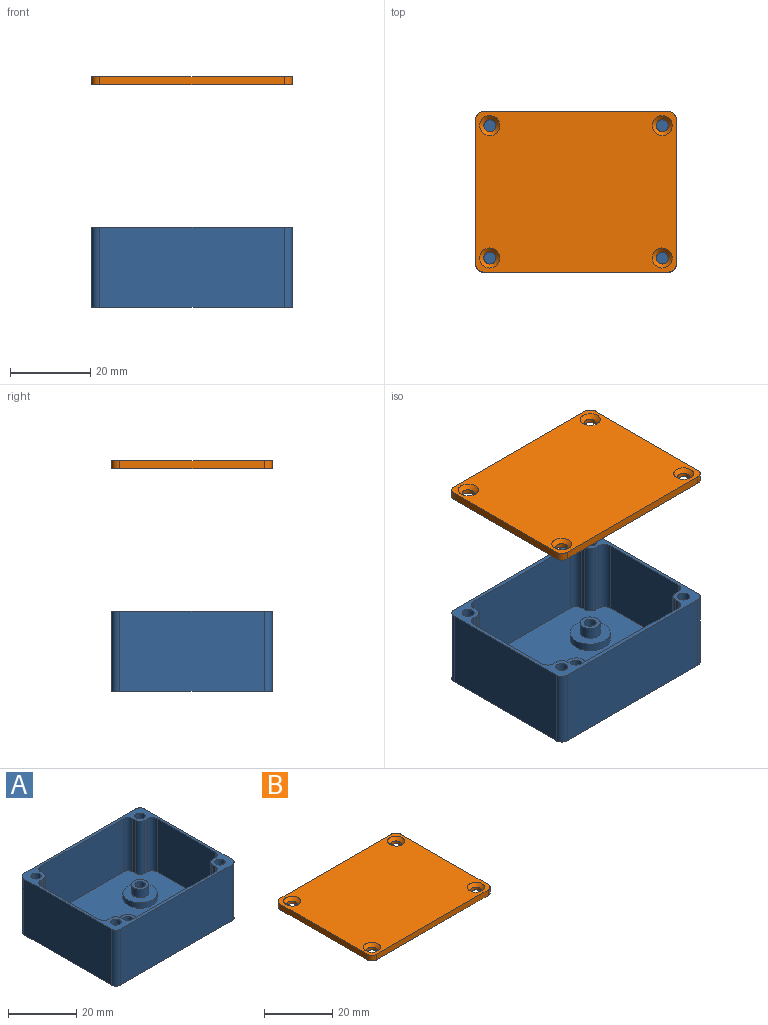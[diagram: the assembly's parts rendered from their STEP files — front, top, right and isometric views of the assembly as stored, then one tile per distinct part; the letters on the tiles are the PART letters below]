
ASSEMBLY  parts=2 mates=1
PART A: 67 faces, bbox 50x40x20 mm
  f0: cylinder r=1.5mm len=4mm, axis (0,0,-1), area 37.7mm2, adj f30,f50
  f1: cylinder r=1.5mm len=4mm, axis (0,0,-1), area 37.7mm2, adj f32,f43
  f2: plane 48x38mm, normal (0,0,1), area 1563.5mm2, adj f3,f4,f5,f6,f13,f14,f15,f16
  f3: plane 24x19mm, normal (-1,0,0), area 456mm2, adj f2,f7,f60,f61
  f4: plane 34x19mm, normal (0,1,0), area 646mm2, adj f2,f7,f56,f58
  f5: plane 34x19mm, normal (0,-1,0), area 646mm2, adj f2,f7,f62,f64
  f6: plane 24x19mm, normal (1,0,0), area 456mm2, adj f2,f7,f57,f66
  f7: plane 50x40mm, normal (0,0,1), area 247.7mm2, adj f3,f4,f5,f6,f8,f9,f10,f11
  f8: plane 46x20mm, normal (0,1,0), area 920mm2, adj f7,f12,f51,f54
  f9: plane 36x20mm, normal (-1,0,0), area 720mm2, adj f7,f12,f51,f52
  f10: plane 46x20mm, normal (0,-1,0), area 920mm2, adj f7,f12,f52,f53
  f11: plane 36x20mm, normal (1,0,0), area 720mm2, adj f7,f12,f53,f54
  f12: plane 50x40mm, normal (0,0,-1), area 1949.8mm2, adj f8,f9,f10,f11,f37,f38,f39,f40
  f13: plane 19x1mm, normal (0,-1,0), area 19mm2, adj f2,f7,f65,f66
  f14: plane 19x1mm, normal (1,0,0), area 19mm2, adj f2,f7,f64,f65
  f15: plane 19x1mm, normal (0,1,0), area 19mm2, adj f2,f7,f55,f57
  f16: plane 19x1mm, normal (1,0,0), area 19mm2, adj f2,f7,f55,f56
  f17: plane 19x1mm, normal (0,-1,0), area 19mm2, adj f2,f7,f61,f63
  f18: plane 19x1mm, normal (-1,0,0), area 19mm2, adj f2,f7,f62,f63
  f19: plane 19x1mm, normal (0,1,0), area 19mm2, adj f2,f7,f59,f60
  f20: plane 19x1mm, normal (-1,0,0), area 19mm2, adj f2,f7,f58,f59
  f21: cylinder r=1.5mm len=10mm, axis (0,0,1), area 94.2mm2, adj f7,f22
  f22: plane 3x3mm, normal (0,0,1), area 7.1mm2, adj f21
  f23: cylinder r=1.5mm len=10mm, axis (0,0,1), area 94.2mm2, adj f7,f24
  f24: plane 3x3mm, normal (0,0,1), area 7.1mm2, adj f23
  f25: cylinder r=1.5mm len=10mm, axis (0,0,1), area 94.2mm2, adj f7,f26
  f26: plane 3x3mm, normal (0,0,1), area 7.1mm2, adj f25
  f27: cylinder r=1.5mm len=10mm, axis (0,0,1), area 94.2mm2, adj f7,f28
  f28: plane 3x3mm, normal (0,0,1), area 7.1mm2, adj f27
  f29: cylinder r=2.5mm len=5mm, axis (0,0,-1), area 47.1mm2, adj f30,f34
  f30: plane 5x5mm, normal (0,0,1), area 12.6mm2, adj f0,f29
  f31: cylinder r=2.5mm len=5mm, axis (0,0,-1), area 47.1mm2, adj f32,f36
  f32: plane 5x5mm, normal (0,0,1), area 12.6mm2, adj f1,f31
  f33: cylinder r=5mm len=10mm, axis (0,0,-1), area 62.8mm2, adj f2,f34
  f34: plane 10x10mm, normal (0,0,1), area 58.9mm2, adj f29,f33
  f35: cylinder r=5mm len=10mm, axis (0,0,-1), area 62.8mm2, adj f2,f36
  f36: plane 10x10mm, normal (0,0,1), area 58.9mm2, adj f31,f35
  f37: plane 3x2mm, normal (1,0,0), area 6mm2, adj f12,f38,f42,f43
  f38: plane 2.6x2mm, normal (0.5,-0.87,0), area 6mm2, adj f12,f37,f39,f43
  f39: plane 2.6x2mm, normal (-0.5,-0.87,0), area 6mm2, adj f12,f38,f40,f43
  f40: plane 3x2mm, normal (-1,0,0), area 6mm2, adj f12,f39,f41,f43
  f41: plane 2.6x2mm, normal (-0.5,0.87,0), area 6mm2, adj f12,f40,f42,f43
  f42: plane 2.6x2mm, normal (0.5,0.87,0), area 6mm2, adj f12,f37,f41,f43
  f43: plane 6x5.2mm, normal (0,0,-1), area 16.3mm2, adj f1,f37,f38,f39,f40,f41,f42
  f44: plane 2.93x2mm, normal (0.98,0.21,0), area 6mm2, adj f12,f45,f49,f50
  f45: plane 2.23x2.01mm, normal (0.67,-0.74,0), area 6mm2, adj f12,f44,f46,f50
  f46: plane 2.85x2mm, normal (-0.31,-0.95,0), area 6mm2, adj f12,f45,f47,f50
  f47: plane 2.93x2mm, normal (-0.98,-0.21,0), area 6mm2, adj f12,f46,f48,f50
  f48: plane 2.23x2.01mm, normal (-0.67,0.74,0), area 6mm2, adj f12,f47,f49,f50
  f49: plane 2.85x2mm, normal (0.31,0.95,0), area 6mm2, adj f12,f44,f48,f50
  f50: plane 5.87x5.71mm, normal (0,0,-1), area 16.3mm2, adj f0,f44,f45,f46,f47,f48,f49
  f51: cylinder r=2mm len=20mm, axis (0,0,1), area 62.8mm2, adj f7,f8,f9,f12
  f52: cylinder r=2mm len=20mm, axis (0,0,-1), area 62.8mm2, adj f7,f9,f10,f12
  f53: cylinder r=2mm len=20mm, axis (0,0,1), area 62.8mm2, adj f7,f10,f11,f12
  f54: cylinder r=2mm len=20mm, axis (0,0,-1), area 62.8mm2, adj f7,f8,f11,f12
  f55: cylinder r=2mm len=19mm, axis (0,0,1), area 59.7mm2, adj f2,f7,f15,f16
  f56: cylinder r=2mm len=19mm, axis (0,0,1), area 59.7mm2, adj f2,f4,f7,f16
  f57: cylinder r=2mm len=19mm, axis (0,0,-1), area 59.7mm2, adj f2,f6,f7,f15
  f58: cylinder r=2mm len=19mm, axis (0,0,-1), area 59.7mm2, adj f2,f4,f7,f20
  f59: cylinder r=2mm len=19mm, axis (0,0,1), area 59.7mm2, adj f2,f7,f19,f20
  f60: cylinder r=2mm len=19mm, axis (0,0,-1), area 59.7mm2, adj f2,f3,f7,f19
  f61: cylinder r=2mm len=19mm, axis (0,0,1), area 59.7mm2, adj f2,f3,f7,f17
  f62: cylinder r=2mm len=19mm, axis (0,0,-1), area 59.7mm2, adj f2,f5,f7,f18
  f63: cylinder r=2mm len=19mm, axis (0,0,1), area 59.7mm2, adj f2,f7,f17,f18
  f64: cylinder r=2mm len=19mm, axis (0,0,1), area 59.7mm2, adj f2,f5,f7,f14
  f65: cylinder r=2mm len=19mm, axis (0,0,1), area 59.7mm2, adj f2,f7,f13,f14
  f66: cylinder r=2mm len=19mm, axis (0,0,1), area 59.7mm2, adj f2,f6,f7,f13
PART B: 18 faces, bbox 50x40x2 mm
  f0: plane 36x2mm, normal (-1,0,0), area 72mm2, adj f4,f5,f14,f17
  f1: plane 46x2mm, normal (0,-1,0), area 92mm2, adj f4,f5,f14,f15
  f2: plane 36x2mm, normal (1,0,0), area 72mm2, adj f4,f5,f15,f16
  f3: plane 46x2mm, normal (0,1,0), area 92mm2, adj f4,f5,f16,f17
  f4: plane 50x40mm, normal (0,0,1), area 1918mm2, adj f0,f1,f2,f3,f10,f11,f12,f13
  f5: plane 50x40mm, normal (0,0,-1), area 1968.3mm2, adj f0,f1,f2,f3,f6,f7,f8,f9
  f6: cylinder r=1.5mm len=3mm, axis (0,0,1), area 9.4mm2, adj f5,f13
  f7: cylinder r=1.5mm len=3mm, axis (0,0,1), area 9.4mm2, adj f5,f12
  f8: cylinder r=1.5mm len=3mm, axis (0,0,1), area 9.4mm2, adj f5,f10
  f9: cylinder r=1.5mm len=3mm, axis (0,0,1), area 9.4mm2, adj f5,f11
  f10: cone r=1.5mm half-angle=45deg, axis (0,0,1), area 17.8mm2, adj f4,f8
  f11: cone r=1.5mm half-angle=45deg, axis (0,0,1), area 17.8mm2, adj f4,f9
  f12: cone r=1.5mm half-angle=45deg, axis (0,0,1), area 17.8mm2, adj f4,f7
  f13: cone r=1.5mm half-angle=45deg, axis (0,0,1), area 17.8mm2, adj f4,f6
  f14: cylinder r=2mm len=2mm, axis (0,0,1), area 6.3mm2, adj f0,f1,f4,f5
  f15: cylinder r=2mm len=2mm, axis (0,0,-1), area 6.3mm2, adj f1,f2,f4,f5
  f16: cylinder r=2mm len=2mm, axis (0,0,1), area 6.3mm2, adj f2,f3,f4,f5
  f17: cylinder r=2mm len=2mm, axis (0,0,-1), area 6.3mm2, adj f0,f3,f4,f5
PLACE A t=(-60.63,-21.07,-21.49)mm fixed
PLACE B rot(axis=(0,0,-1),0deg) t=(-138.23,-19.6,34.05)mm
MATE slider A.f25 <-> B.f8  axis (0,0,1) through (-81.12,6.11,-1.49)mm
